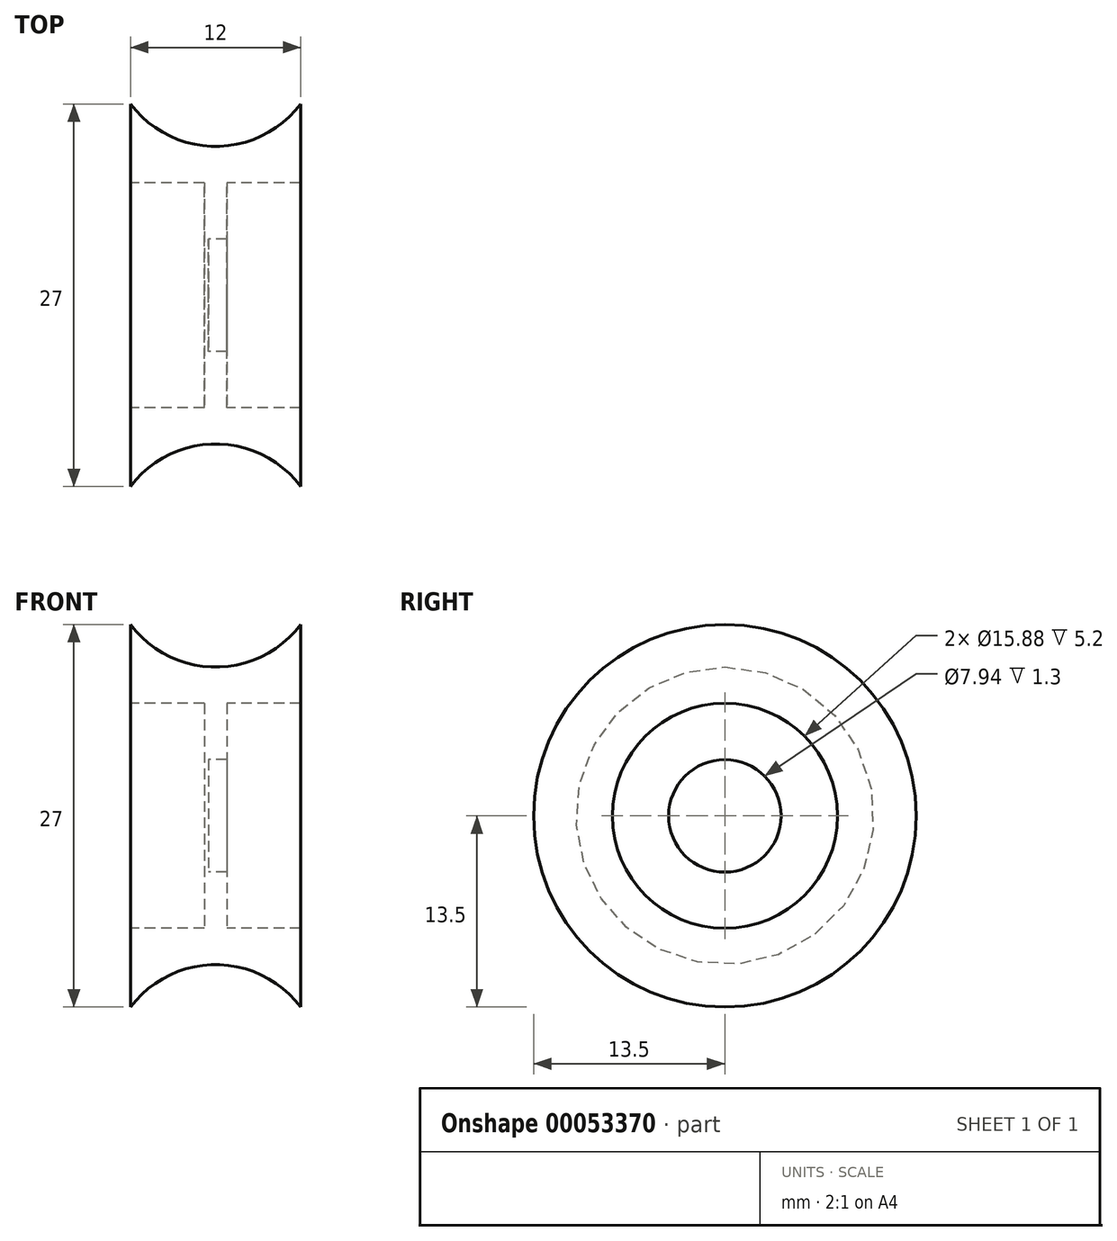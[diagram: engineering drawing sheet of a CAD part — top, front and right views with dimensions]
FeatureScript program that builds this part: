
annotation { "Feature Type Name" : "Feature", "Feature Type Description" : "" }
export const myFeature = defineFeature(function(context is Context, id is Id, definition is map)
    precondition{}
    {
        {
            var Q0;
            Q0=qCreatedBy(makeId("Front.planeOp"),FACE);
            var sketch = newSketch(context, id + "F0", { "sketchPlane" : qUnion([Q0])});
            skLineSegment(sketch, "E0", {"start": v(0, 14.34) * mm, "end": v(0, -18.66) * mm, "construction": true});
            skLineSegment(sketch, "E1", {"start": v(-23.02, 0) * mm, "end": v(22.12, 0) * mm, "construction": true});
            skCircle(sketch, "E2", {"center": v(0, 18) * mm, "radius": 7.5 * mm});
            skLineSegment(sketch, "E3", {"start": v(-11.68, 18) * mm, "end": v(11.24, 18) * mm});
            skLineSegment(sketch, "E4", {"start": v(-6, 18) * mm, "end": v(-6, 0) * mm});
            skLineSegment(sketch, "E5.MirrorCS", {"start": v(6, 18) * mm, "end": v(6, 0) * mm});
            skLineSegment(sketch, "E6", {"start": v(-6, 7.94) * mm, "end": v(-0.8, 7.94) * mm});
            skLineSegment(sketch, "E7", {"start": v(-0.8, 7.94) * mm, "end": v(-0.8, 0) * mm});
            skLineSegment(sketch, "E8.MirrorCS", {"start": v(0.8, 7.94) * mm, "end": v(0.8, 0) * mm});
            skLineSegment(sketch, "E9.MirrorCS", {"start": v(6, 7.94) * mm, "end": v(0.8, 7.94) * mm});
            skLineSegment(sketch, "E10.rect.bottom", {"start": v(0.8, 3.97) * mm, "end": v(-0.5, 3.97) * mm});
            skPoint(sketch, "E10.rect.middle", {"position": v(0, 0) * mm});
            skLineSegment(sketch, "E11", {"start": v(-0.5, 3.97) * mm, "end": v(-0.5, 0) * mm});
            skLineSegment(sketch, "E12", {"start": v(0.8, 0) * mm, "end": v(-0.8, 0) * mm});
            skSolve(sketch);
        }
        {
            var Q0;
            {var subQ0=sQuery(id+"F0.wireOp",EDGE,"E6");Q0=makeQuery(id+"F0.imprint","IMPRINT",FACE,{"disambiguationData":[TD([[makeQuery(id+"F0.imprint","IMPRINT",EDGE,{"derivedFrom":subQ0}),1.0]])]});}
            var Q1;
            {var subQ0=sQuery(id+"F0.wireOp",EDGE,"ca122a81-0204-486e-bc16-6ec66c693c47.left");Q1=makeQuery(id+"F0.imprint","IMPRINT",FACE,{"disambiguationData":[TD([[makeQuery(id+"F0.imprint","IMPRINT",EDGE,{"derivedFrom":subQ0}),-1.0]])]});}
            var Q2;
            Q2=sQuery(id+"F0.wireOp",EDGE,"E1");
            revolve(context, id + "F1", {"entities" : qUnion([Q0, Q1]), "axis" : qUnion([Q2]), "revolveType" : RevolveType.FULL});
        }
    });
